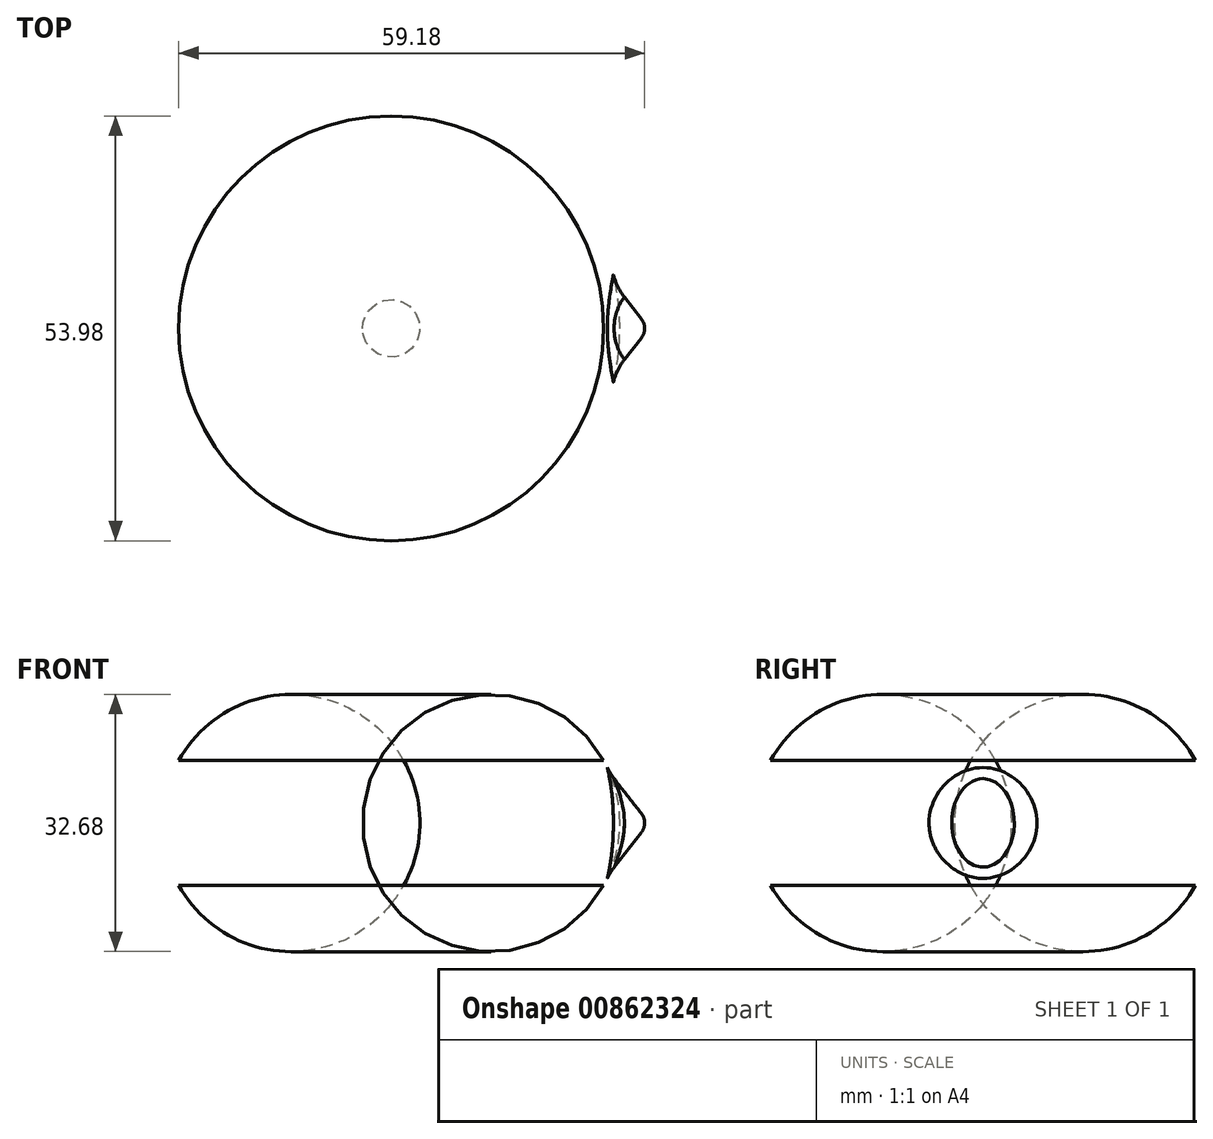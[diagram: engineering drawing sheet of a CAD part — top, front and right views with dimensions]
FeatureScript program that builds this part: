
annotation { "Feature Type Name" : "Feature", "Feature Type Description" : "" }
export const myFeature = defineFeature(function(context is Context, id is Id, definition is map)
    precondition{}
    {
        {
            var Q0;
            Q0=qCreatedBy(makeId("Front.planeOp"),FACE);
            var sketch = newSketch(context, id + "F0", { "sketchPlane" : qUnion([Q0])});
            skLineSegment(sketch, "E0.bottom", {"start": v(0, 7.94) * mm, "end": v(26.99, 7.94) * mm});
            skLineSegment(sketch, "E0.top", {"start": v(0, -7.94) * mm, "end": v(26.99, -7.94) * mm});
            skLineSegment(sketch, "E0.left", {"start": v(0, 7.94) * mm, "end": v(0, -7.94) * mm});
            skArc(sketch, "E1", {"start": v(26.99, -7.94) * mm, "mid": v(29.04, 0) * mm, "end": v(26.99, 7.94) * mm});
            skLineSegment(sketch, "E2", {"start": v(0, 0) * mm, "end": v(0, 7.94) * mm, "construction": true});
            skSolve(sketch);
        }
        {
            var Q0;
            Q0 = qSketchRegion(id + "F0", true);
            var Q1;
            Q1=sQuery(id+"F0.wireOp",EDGE,"E0.left");
            revolve(context, id + "F1", {"surfaceOperationType" : NewSurfaceOperationType.NEW, "entities" : qUnion([Q0]), "axis" : qUnion([Q1]), "revolveType" : RevolveType.FULL});
        }
        {
            var Q0;
            Q0=qCreatedBy(makeId("Front.planeOp"),FACE);
            var sketch = newSketch(context, id + "F2", { "sketchPlane" : qUnion([Q0])});
            skLineSegment(sketch, "E3.0", {"start": v(-26.99, 7.94) * mm, "end": v(26.99, 7.94) * mm, "construction": true});
            skLineSegment(sketch, "E4.0", {"start": v(-26.99, -7.94) * mm, "end": v(26.99, -7.94) * mm, "construction": true});
            skLineSegment(sketch, "E5", {"start": v(26.99, 7.94) * mm, "end": v(26.99, -7.94) * mm, "construction": true});
            skLineSegment(sketch, "E6", {"start": v(26.99, 0) * mm, "end": v(29.04, 0) * mm, "construction": true});
            skLineSegment(sketch, "E7", {"start": v(26.99, 6.35) * mm, "end": v(27.76, 6.35) * mm});
            skLineSegment(sketch, "E8", {"start": v(27.76, 6.35) * mm, "end": v(31.77, 1.21) * mm});
            skArc(sketch, "E9", {"start": v(26.99, -7.94) * mm, "mid": v(29.04, 0) * mm, "end": v(26.99, 7.94) * mm, "construction": true});
            skLineSegment(sketch, "E10", {"start": v(26.99, 6.35) * mm, "end": v(26.99, 0) * mm});
            skLineSegment(sketch, "E11", {"start": v(26.99, 0) * mm, "end": v(32.2, 0) * mm});
            skArc(sketch, "E12", {"start": v(32.2, 0) * mm, "mid": v(32.08, 0.64) * mm, "end": v(31.77, 1.21) * mm});
            skPoint(sketch, "E13", {"position": v(29.04, 0) * mm});
            skPoint(sketch, "E14.orphan", {"position": v(31.77, -1.21) * mm});
            skLineSegment(sketch, "E15.trimOffspring", {"start": v(32.72, 0) * mm, "end": v(38.46, 0) * mm, "construction": true});
            skLineSegment(sketch, "E16.trimOffspring", {"start": v(30.22, 0) * mm, "end": v(32.2, 0) * mm, "construction": true});
            skSolve(sketch);
        }
        {
            var Q0;
            Q0 = qSketchRegion(id + "F2", true);
            var Q1;
            Q1=sQuery(id+"F2.wireOp",EDGE,"E6");
            revolve(context, id + "F3", {"operationType" : NewBodyOperationType.ADD, "surfaceOperationType" : NewSurfaceOperationType.NEW, "entities" : qUnion([Q0]), "axis" : qUnion([Q1]), "revolveType" : RevolveType.FULL});
        }
        {
            var Q0;
            Q0=makeQuery(id+"F3.opRevolve","SWEPT_FACE",FACE,{"disambiguationData":[OSD([sQuery(id+"F2.wireOp",EDGE,"E8")])]});
            fillet(context, id + "F4", {"entities" : qUnion([Q0]), "radius" : 7.62 * mm, "tangentPropagation" : true, "allowEdgeOverflow" : false});
        }
    });
